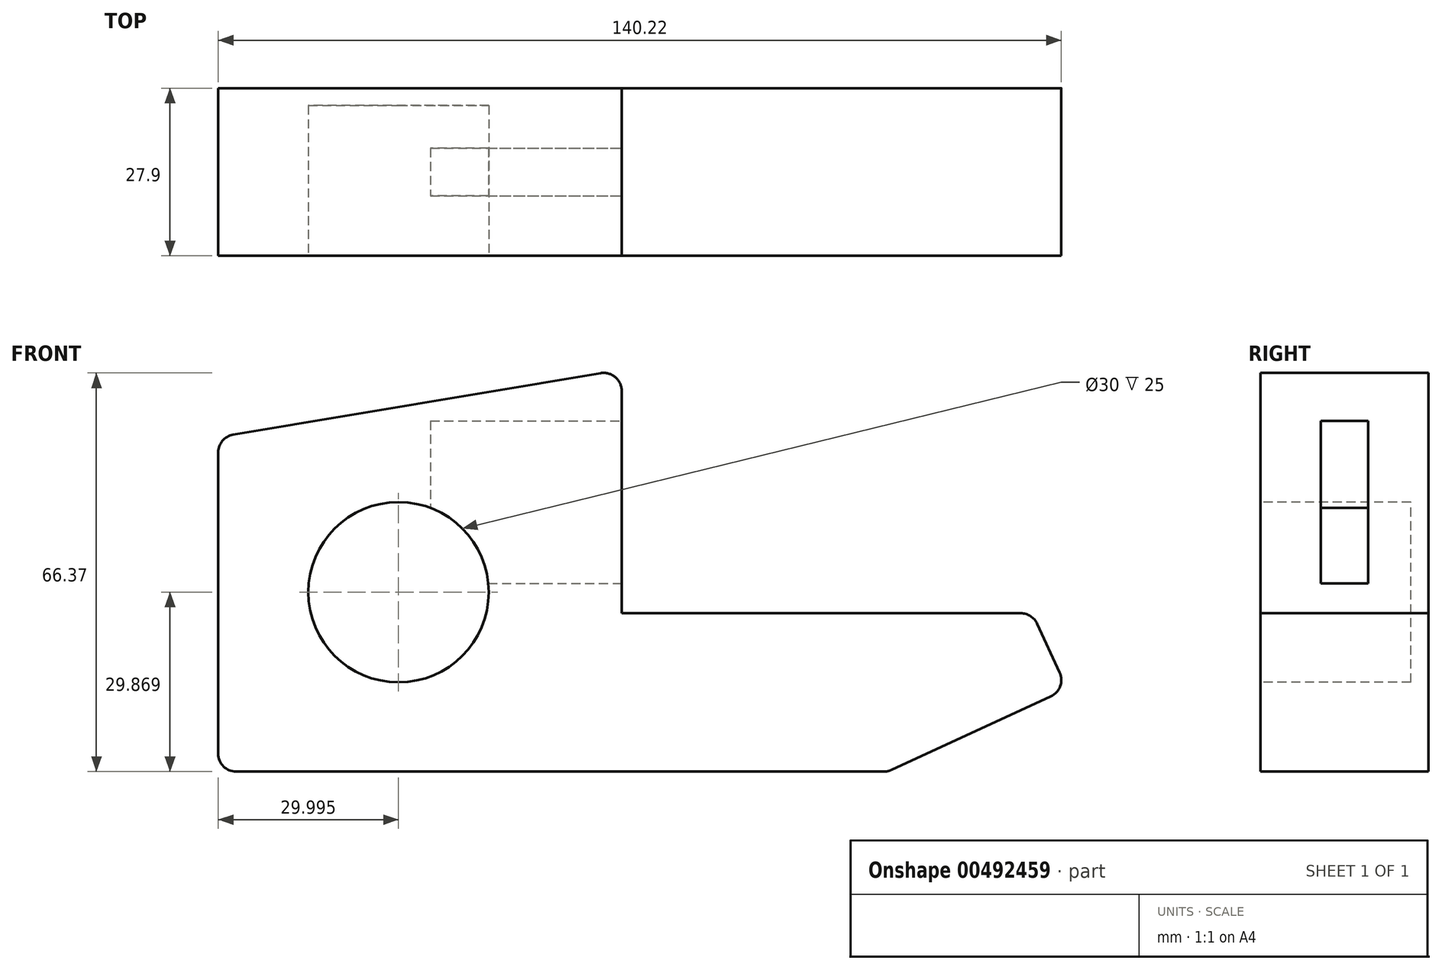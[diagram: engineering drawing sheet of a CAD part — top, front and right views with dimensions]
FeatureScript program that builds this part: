
annotation { "Feature Type Name" : "Feature", "Feature Type Description" : "" }
export const myFeature = defineFeature(function(context is Context, id is Id, definition is map)
    precondition{}
    {
        {
            var Q0;
            Q0=qCreatedBy(makeId("Front.planeOp"),FACE);
            var sketch = newSketch(context, id + "F0", { "sketchPlane" : qUnion([Q0])});
            skLineSegment(sketch, "E0", {"start": v(-51.6, 32.59) * mm, "end": v(-51.6, -23.08) * mm});
            skLineSegment(sketch, "E1", {"start": v(-51.6, -23.08) * mm, "end": v(59.74, -23.08) * mm});
            skLineSegment(sketch, "E2", {"start": v(59.74, -23.08) * mm, "end": v(89.61, -9.31) * mm});
            skLineSegment(sketch, "E3", {"start": v(89.61, -9.31) * mm, "end": v(83.8, 3.27) * mm});
            skLineSegment(sketch, "E4", {"start": v(83.8, 3.27) * mm, "end": v(15.52, 3.27) * mm});
            skLineSegment(sketch, "E5", {"start": v(15.52, 3.27) * mm, "end": v(15.52, 43.84) * mm});
            skLineSegment(sketch, "E6", {"start": v(15.52, 43.84) * mm, "end": v(-51.6, 32.59) * mm});
            skSolve(sketch);
        }
        {
            var Q0;
            Q0 = qSketchRegion(id + "F0", true);
            extrude(context, id + "F1", {"entities" : qUnion([Q0]), "depth" : 27.9 * mm});
        }
        {
            var Q0;
            Q0=makeQuery(id+"F1.opExtrude","CAP_FACE",FACE,{"disambiguationData":[OSD([sQuery(id+"F0.wireOp",EDGE,"E0"),sQuery(id+"F0.wireOp",EDGE,"E1"),sQuery(id+"F0.wireOp",EDGE,"E2"),sQuery(id+"F0.wireOp",EDGE,"E3"),sQuery(id+"F0.wireOp",EDGE,"E4"),sQuery(id+"F0.wireOp",EDGE,"E5"),sQuery(id+"F0.wireOp",EDGE,"E6")])],"isStart":false});
            var sketch = newSketch(context, id + "F2", { "sketchPlane" : qUnion([Q0])});
            skCircle(sketch, "E7", {"center": v(-21.6, 6.79) * mm, "radius": 15 * mm});
            skSolve(sketch);
        }
        {
            var Q0;
            Q0 = qSketchRegion(id + "F2", true);
            extrude(context, id + "F3", {"entities" : qUnion([Q0]), "operationType" : NewBodyOperationType.REMOVE, "oppositeDirection" : true, "depth" : 25 * mm});
        }
        {
            var Q0;
            Q0=makeQuery(id+"F1.opExtrude","SWEPT_EDGE",EDGE,{"disambiguationData":[OSD([sQuery(id+"F0.wireOp",EDGE,"E5"),sQuery(id+"F0.wireOp",EDGE,"E6")])]});
            var Q1;
            Q1=makeQuery(id+"F1.opExtrude","SWEPT_EDGE",EDGE,{"disambiguationData":[OSD([sQuery(id+"F0.wireOp",EDGE,"E3"),sQuery(id+"F0.wireOp",EDGE,"E4")])]});
            var Q2;
            Q2=makeQuery(id+"F1.opExtrude","SWEPT_EDGE",EDGE,{"disambiguationData":[OSD([sQuery(id+"F0.wireOp",EDGE,"E2"),sQuery(id+"F0.wireOp",EDGE,"E3")])]});
            var Q3;
            Q3=makeQuery(id+"F1.opExtrude","SWEPT_EDGE",EDGE,{"disambiguationData":[OSD([sQuery(id+"F0.wireOp",EDGE,"E1"),sQuery(id+"F0.wireOp",EDGE,"E2")])]});
            var Q4;
            Q4=makeQuery(id+"F1.opExtrude","SWEPT_EDGE",EDGE,{"disambiguationData":[OSD([sQuery(id+"F0.wireOp",EDGE,"E0"),sQuery(id+"F0.wireOp",EDGE,"E1")])]});
            var Q5;
            Q5=makeQuery(id+"F1.opExtrude","SWEPT_EDGE",EDGE,{"disambiguationData":[OSD([sQuery(id+"F0.wireOp",EDGE,"E0"),sQuery(id+"F0.wireOp",EDGE,"E6")])]});
            fillet(context, id + "F4", {"entities" : qUnion([Q0, Q1, Q2, Q3, Q4, Q5]), "radius" : 3 * mm, "tangentPropagation" : true, "allowEdgeOverflow" : false});
        }
        {
            var Q0;
            Q0=makeQuery(id+"F1.opExtrude","SWEPT_FACE",FACE,{"disambiguationData":[OSD([sQuery(id+"F0.wireOp",EDGE,"E5")])]});
            var sketch = newSketch(context, id + "F5", { "sketchPlane" : qUnion([Q0])});
            skLineSegment(sketch, "E8.bottom", {"start": v(-17.9, 35.3) * mm, "end": v(-10, 35.3) * mm});
            skLineSegment(sketch, "E8.top", {"start": v(-17.9, 8.27) * mm, "end": v(-10, 8.27) * mm});
            skLineSegment(sketch, "E8.left", {"start": v(-17.9, 35.3) * mm, "end": v(-17.9, 8.27) * mm});
            skLineSegment(sketch, "E8.right", {"start": v(-10, 35.3) * mm, "end": v(-10, 8.27) * mm});
            skSolve(sketch);
        }
        {
            var Q0;
            Q0 = qSketchRegion(id + "F5", true);
            extrude(context, id + "F6", {"entities" : qUnion([Q0]), "operationType" : NewBodyOperationType.REMOVE, "oppositeDirection" : true, "depth" : 31.8 * mm, "offsetDistance" : 25 * mm});
        }
    });
